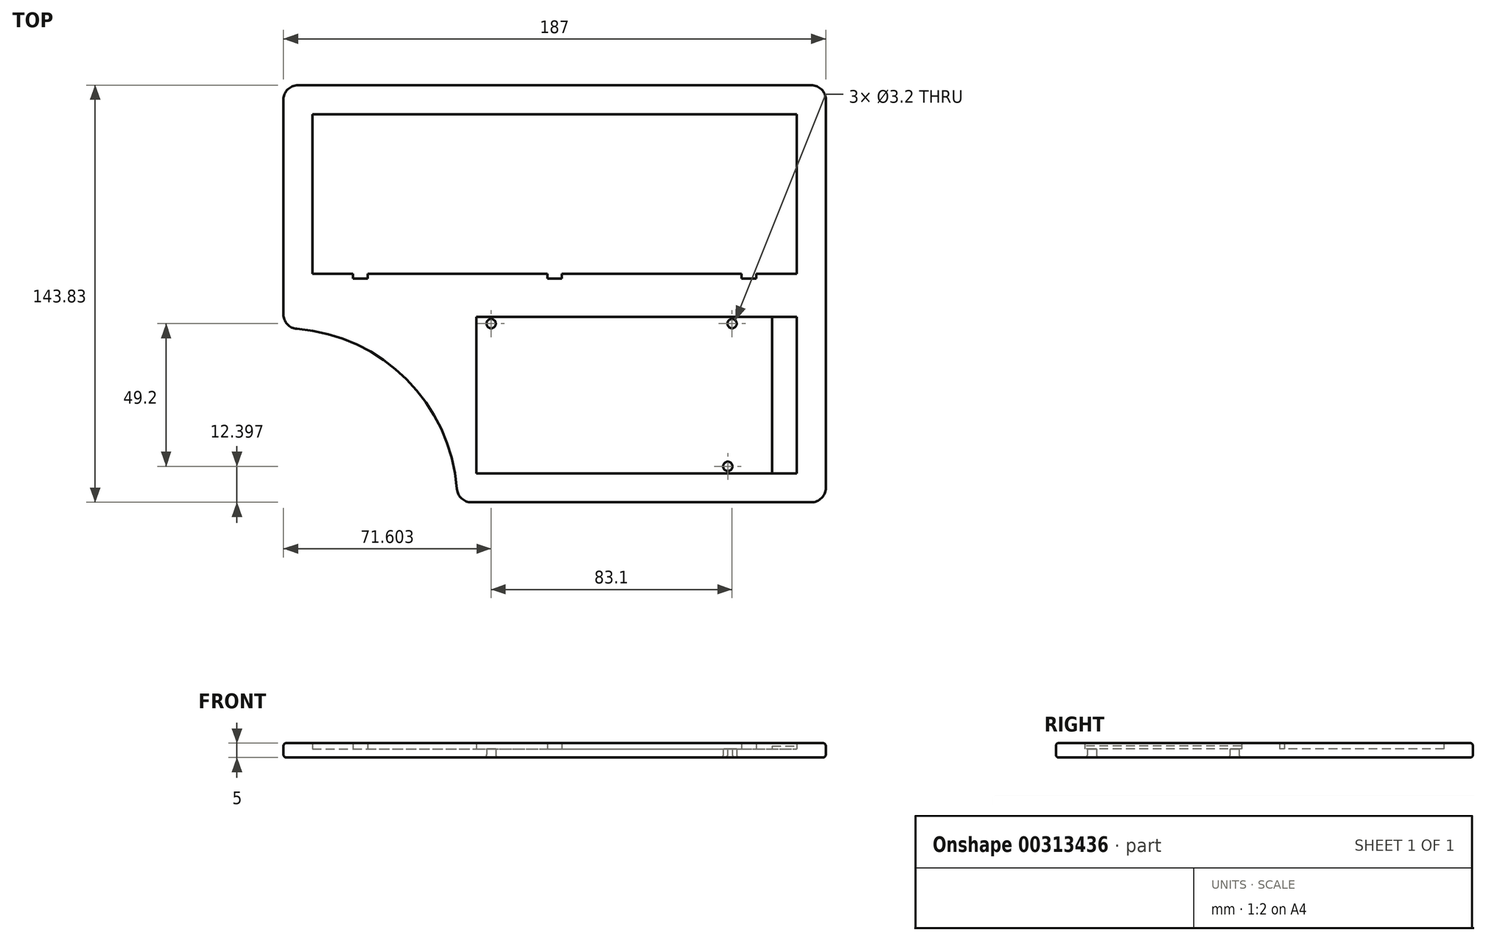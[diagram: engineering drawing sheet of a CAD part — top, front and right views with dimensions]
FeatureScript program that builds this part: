
annotation { "Feature Type Name" : "Feature", "Feature Type Description" : "" }
export const myFeature = defineFeature(function(context is Context, id is Id, definition is map)
    precondition{}
    {
        {
            var Q0;
            Q0=qCreatedBy(makeId("Top.planeOp"),FACE);
            var sketch = newSketch(context, id + "F0", { "sketchPlane" : qUnion([Q0])});
            skLineSegment(sketch, "E0.bottom", {"start": v(-83.14, 76.39) * mm, "end": v(83.86, 76.39) * mm});
            skLineSegment(sketch, "E0.top", {"start": v(-83.14, 21.39) * mm, "end": v(-69.14, 21.39) * mm});
            skLineSegment(sketch, "E0.left", {"start": v(-83.14, 76.39) * mm, "end": v(-83.14, 21.39) * mm});
            skLineSegment(sketch, "E0.right", {"start": v(83.86, 76.39) * mm, "end": v(83.86, 21.39) * mm});
            skLineSegment(sketch, "E1.bottom", {"start": v(-26.64, 6.56) * mm, "end": v(75.36, 6.56) * mm});
            skLineSegment(sketch, "E1.top", {"start": v(-26.64, -47.44) * mm, "end": v(75.36, -47.44) * mm});
            skLineSegment(sketch, "E1.left", {"start": v(-26.64, 6.56) * mm, "end": v(-26.64, -47.44) * mm});
            skLineSegment(sketch, "E1.right", {"start": v(75.36, 6.56) * mm, "end": v(75.36, -47.44) * mm});
            skLineSegment(sketch, "E2.bottom", {"start": v(-26.64, 6.56) * mm, "end": v(83.86, 6.56) * mm});
            skLineSegment(sketch, "E2.top", {"start": v(-26.64, -47.44) * mm, "end": v(83.86, -47.44) * mm});
            skLineSegment(sketch, "E2.right", {"start": v(83.86, 6.56) * mm, "end": v(83.86, -47.44) * mm});
            skLineSegment(sketch, "E3.bottom", {"start": v(-93.14, 86.39) * mm, "end": v(93.86, 86.39) * mm});
            skLineSegment(sketch, "E3.top", {"start": v(-33.14, -57.44) * mm, "end": v(93.86, -57.44) * mm});
            skLineSegment(sketch, "E3.left", {"start": v(-93.14, 86.39) * mm, "end": v(-93.14, 2.56) * mm});
            skLineSegment(sketch, "E3.right", {"start": v(93.86, 86.39) * mm, "end": v(93.86, -57.44) * mm});
            skCircle(sketch, "E4", {"center": v(61.56, 4.16) * mm, "radius": 1.6 * mm});
            skCircle(sketch, "E5", {"center": v(60.06, -45.04) * mm, "radius": 1.6 * mm});
            skCircle(sketch, "E6", {"center": v(-21.54, 4.16) * mm, "radius": 1.6 * mm});
            skLineSegment(sketch, "E7.top", {"start": v(64.86, 19.65) * mm, "end": v(69.86, 19.65) * mm});
            skLineSegment(sketch, "E7.left", {"start": v(64.86, 21.39) * mm, "end": v(64.86, 19.65) * mm});
            skLineSegment(sketch, "E7.right", {"start": v(69.86, 21.39) * mm, "end": v(69.86, 19.65) * mm});
            skLineSegment(sketch, "E8.top", {"start": v(-2.14, 19.65) * mm, "end": v(2.86, 19.65) * mm});
            skLineSegment(sketch, "E8.left", {"start": v(-2.14, 21.39) * mm, "end": v(-2.14, 19.65) * mm});
            skLineSegment(sketch, "E8.right", {"start": v(2.86, 21.39) * mm, "end": v(2.86, 19.65) * mm});
            skLineSegment(sketch, "E9.top", {"start": v(-69.14, 19.65) * mm, "end": v(-64.14, 19.65) * mm});
            skLineSegment(sketch, "E9.left", {"start": v(-69.14, 21.39) * mm, "end": v(-69.14, 19.65) * mm});
            skLineSegment(sketch, "E9.right", {"start": v(-64.14, 21.39) * mm, "end": v(-64.14, 19.65) * mm});
            skLineSegment(sketch, "E10.trimOffspring", {"start": v(-64.14, 21.39) * mm, "end": v(-2.14, 21.39) * mm});
            skLineSegment(sketch, "E11.trimOffspring", {"start": v(2.86, 21.39) * mm, "end": v(64.86, 21.39) * mm});
            skLineSegment(sketch, "E12.trimOffspring", {"start": v(69.86, 21.39) * mm, "end": v(83.86, 21.39) * mm});
            skArc(sketch, "E13", {"start": v(-33.14, -57.44) * mm, "mid": v(-50.71, -15.02) * mm, "end": v(-93.14, 2.56) * mm});
            skSolve(sketch);
        }
        {
            var Q0;
            Q0=makeQuery(id+"F0.imprint","IMPRINT",FACE,{"disambiguationData":[TD([[makeQuery(id+"F0.imprint","IMPRINT",EDGE,{"derivedFrom":sQuery(id+"F0.wireOp",EDGE,"E0.bottom")}),1.0]])]});
            extrude(context, id + "F1", {"entities" : qUnion([Q0]), "depth" : 5 * mm});
        }
        {
            var Q0;
            Q0=makeQuery(id+"F0.imprint","IMPRINT",FACE,{"disambiguationData":[TD([[makeQuery(id+"F0.imprint","IMPRINT",EDGE,{"derivedFrom":sQuery(id+"F0.wireOp",EDGE,"E0.bottom")}),-1.0]])]});
            var Q1;
            {var subQ1=sQuery(id+"F0.wireOp",EDGE,"E1.right");Q1=makeQuery(id+"F0.imprint","IMPRINT",FACE,{"disambiguationData":[TD([[makeQuery(id+"F0.imprint","IMPRINT",EDGE,{"derivedFrom":subQ1}),-1.0]])]});}
            extrude(context, id + "F2", {"entities" : qUnion([Q0, Q1]), "operationType" : NewBodyOperationType.ADD, "depth" : 3 * mm});
        }
        {
            var Q0;
            {var subQ0=sQuery(id+"F0.wireOp",EDGE,"E1.right");Q0=makeQuery(id+"F0.imprint","IMPRINT",FACE,{"disambiguationData":[TD([[makeQuery(id+"F0.imprint","IMPRINT",EDGE,{"derivedFrom":subQ0}),1.0]])]});}
            extrude(context, id + "F3", {"entities" : qUnion([Q0]), "operationType" : NewBodyOperationType.ADD, "depth" : 4 * mm});
        }
        {
            var Q0;
            Q0=makeQuery(id+"F1.opExtrude","SWEPT_EDGE",EDGE,{"disambiguationData":[OSD([sQuery(id+"F0.wireOp",EDGE,"E3.top"),sQuery(id+"F0.wireOp",EDGE,"E3.left")])]});
            var Q1;
            Q1=makeQuery(id+"F1.opExtrude","SWEPT_EDGE",EDGE,{"disambiguationData":[OSD([sQuery(id+"F0.wireOp",EDGE,"E3.top"),sQuery(id+"F0.wireOp",EDGE,"E3.right")])]});
            var Q2;
            Q2=makeQuery(id+"F1.opExtrude","SWEPT_EDGE",EDGE,{"disambiguationData":[OSD([sQuery(id+"F0.wireOp",EDGE,"E3.bottom"),sQuery(id+"F0.wireOp",EDGE,"E3.right")])]});
            var Q3;
            Q3=makeQuery(id+"F1.opExtrude","SWEPT_EDGE",EDGE,{"disambiguationData":[OSD([sQuery(id+"F0.wireOp",EDGE,"E3.bottom"),sQuery(id+"F0.wireOp",EDGE,"E3.left")])]});
            fillet(context, id + "F4", {"entities" : qUnion([Q0, Q1, Q2, Q3]), "radius" : 5 * mm, "tangentPropagation" : true, "allowEdgeOverflow" : false});
        }
        {
            var Q0;
            Q0=makeQuery(id+"F1.opExtrude","CAP_EDGE",EDGE,{"disambiguationData":[OSD([sQuery(id+"F0.wireOp",EDGE,"E3.right")])],"isStart":false});
            var Q1;
            {var subQ0=sQuery(id+"F0.wireOp",EDGE,"E2.right");var subQ1=sQuery(id+"F0.wireOp",EDGE,"E1.left");var subQ2=sQuery(id+"F0.wireOp",EDGE,"E2.top");var subQ3=sQuery(id+"F0.wireOp",EDGE,"E2.bottom");var subQ4=sQuery(id+"F0.wireOp",EDGE,"E12.trimOffspring");var subQ5=sQuery(id+"F0.wireOp",EDGE,"E11.trimOffspring");var subQ6=sQuery(id+"F0.wireOp",EDGE,"E10.trimOffspring");var subQ7=sQuery(id+"F0.wireOp",EDGE,"E9.right");var subQ8=sQuery(id+"F0.wireOp",EDGE,"E9.left");var subQ9=sQuery(id+"F0.wireOp",EDGE,"E9.top");var subQ10=sQuery(id+"F0.wireOp",EDGE,"E8.right");var subQ11=sQuery(id+"F0.wireOp",EDGE,"E8.left");var subQ12=sQuery(id+"F0.wireOp",EDGE,"E8.top");var subQ13=sQuery(id+"F0.wireOp",EDGE,"E7.right");var subQ14=sQuery(id+"F0.wireOp",EDGE,"E7.left");var subQ15=sQuery(id+"F0.wireOp",EDGE,"E7.top");var subQ16=sQuery(id+"F0.wireOp",EDGE,"E0.right");var subQ17=sQuery(id+"F0.wireOp",EDGE,"E0.left");var subQ18=sQuery(id+"F0.wireOp",EDGE,"E0.top");var subQ19=sQuery(id+"F0.wireOp",EDGE,"E0.bottom");Q1=makeQuery(id+"F2.boolean.opBoolean","MERGE",FACE,{"derivedFrom":[makeQuery(id+"F1.opExtrude","CAP_FACE",FACE,{"disambiguationData":[OSD([subQ19,subQ18,subQ17,subQ16,subQ3,subQ2,subQ1,subQ0,sQuery(id+"F0.wireOp",EDGE,"E3.bottom"),sQuery(id+"F0.wireOp",EDGE,"E3.top"),sQuery(id+"F0.wireOp",EDGE,"E3.left"),sQuery(id+"F0.wireOp",EDGE,"E3.right"),subQ15,subQ14,subQ13,subQ12,subQ11,subQ10,subQ9,subQ8,subQ7,subQ6,subQ5,subQ4])],"isStart":true}),makeQuery(id+"F2.opExtrude","CAP_FACE",FACE,{"disambiguationData":[OSD([subQ19,subQ18,subQ17,subQ16,subQ15,subQ14,subQ13,subQ12,subQ11,subQ10,subQ9,subQ8,subQ7,subQ6,subQ5,subQ4])],"isStart":true}),makeQuery(id+"F2.opExtrude","CAP_FACE",FACE,{"disambiguationData":[OSD([subQ3,subQ2,subQ1,subQ0,sQuery(id+"F0.wireOp",EDGE,"E4"),sQuery(id+"F0.wireOp",EDGE,"E5"),sQuery(id+"F0.wireOp",EDGE,"E6")])],"isStart":true})]});}
            fillet(context, id + "F5", {"entities" : qUnion([Q0, Q1]), "radius" : 1 * mm, "tangentPropagation" : true, "allowEdgeOverflow" : false});
        }
    });
